# Revit family: 0047438 Feilo Sylvania Lighting Fixtures START FLAT PANEL LED 1200 NW
name_source: partatom
category: Lighting Fixtures
revit_build: Autodesk Revit 2017 (Build: 20190507_1515(x64)
units: mm (PartAtom-declared; Revit-internal decimal feet)

## family parameters
Cut with Voids When Loaded = No
Host = Face
Light Source = Yes
OmniClass Number = 23.80.70.00
OmniClass Title = Lighting
Part Type = Normal
Room Calculation Point = No
Round Connector Dimension = Use Diameter
Shared = No

## types (1)
- 0047438 START FLAT PANEL LED 1200 NW
    AccessoryMaterial = <By Category>
    Apparent Load = 45 VA
    Assembly Code = D5020200
    AssetType = Fixed
    BodyMaterial = Body-Sylvania-StartFlat1200x300-AluminiumFrame
    ClassificationName = Uniclass2015
    ClassificationValue = EF_70_80
    Color Filter = 16777215
    Cost = 0 $
    Default Elevation = 1219 mm
    Description = Edge lit LED flat panel. 45W Neutral White 4000K 1200x300mm, 3700 lumens 82lm/W, 40,000hrs lifetime (L70), 10.5mm height, PMMA diffuser, aluminium frame, steel body, electronic non-dimmable driver.
    DiffuserMaterial = Diffuser-Sylvania-StartFlat1200x300-PMMA
    Dimming Lamp Color Temperature Shift = <None>
    DocumentationLiterature = http://www.sylvania-lighting.com
    DurationUnit = hours
    ElectricShockClassification = Class II
    Emit Shape Visible in Rendering = No
    Emit from Rectangle Length = 1152 mm
    Emit from Rectangle Width = 251 mm  [stored 0.823491 ft]
    ExpectedLife = 50000
    IfcExportAs = IfcLightFixtureType
    IfcExportType = IfcLightFixtureType
    ImpactProtectionIndex = IK05
    IngressProtection = IP20
    InputVoltage = 220-240V~
    Keynote = 16500
    Lamp = LED
    LampColourRenderingIndex = 0
    LampColourTemperature = 4000 K
    LampNominalLuminous = 3700 lm
    LampsType = LED
    LightOutputRatio = 100
    LuminousEfficacy = 82 lm/W
    Manufacturer = Feilo Sylvania
    ManufacturerName = Feilo Sylvania
    Material = powder coated steel housing, acrylic pmma diffuser
    Model = START FLAT PANEL LED 1200 NW
    ModelNumber = 0047438
    ModelReference = START FLAT PANEL LED 1200 NW
    Name = START FLAT PANEL LED 1200 NW
    NominalDepth = 295 mm
    NominalHeight = 11 mm
    NominalLength = 1195 mm
    Photometric Web File = 0047438.ies
    PowerConsumption = 45 W
    PowerFactor = 0
    ReflectorMaterial = <By Category>
    Tilt Angle = -90.00°
    Type Image = <None>
    TypeName = START FLAT PANEL LED 1200 NW
    URL = http://www.sylvania-lighting.com
    Voltage = 230 V
    Weight = 6.38 kg

note: [stored X ft] marks values corroborated as IEEE doubles in the binary element streams (Revit-internal decimal feet)

## geometry (parser evidence)
native form markers: Sweep x3
no freeform markers — native parametric forms only
